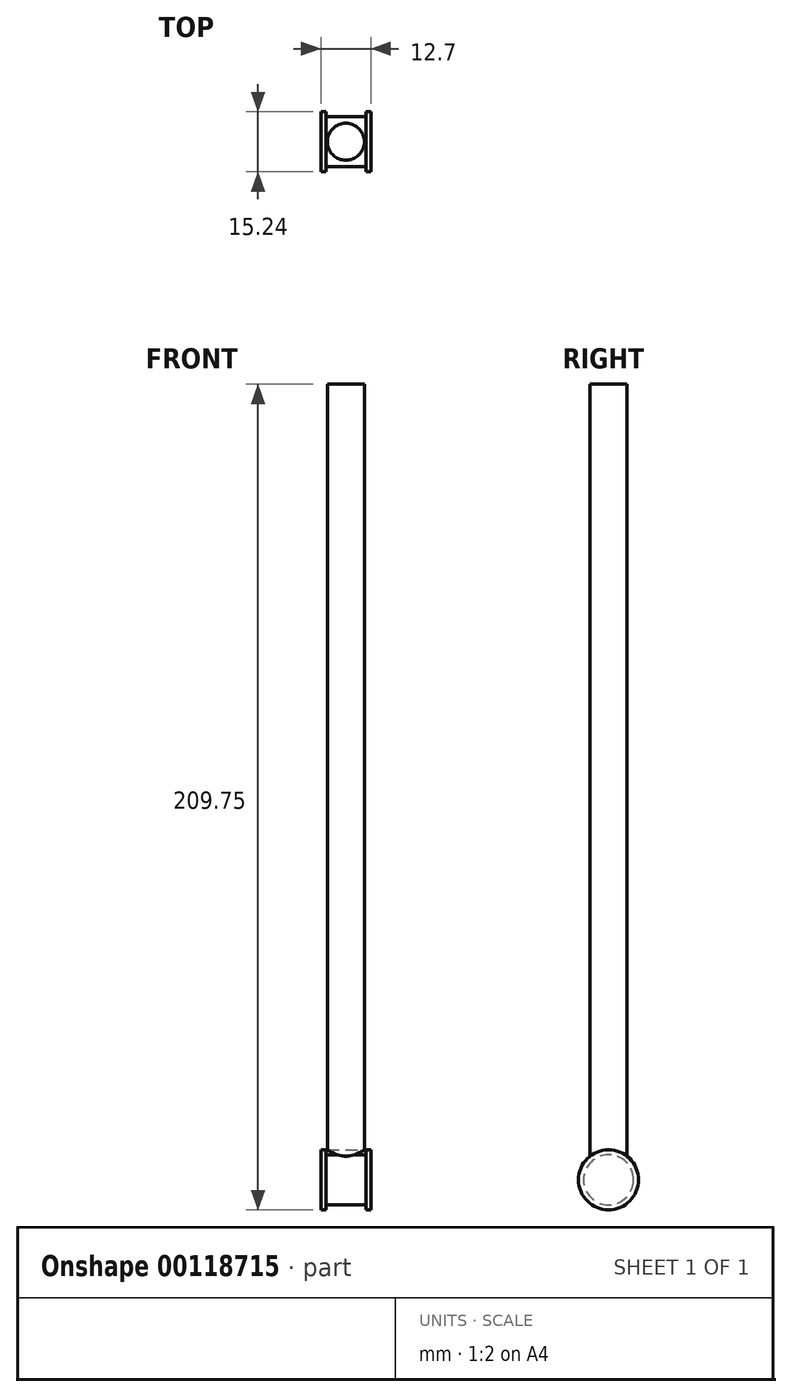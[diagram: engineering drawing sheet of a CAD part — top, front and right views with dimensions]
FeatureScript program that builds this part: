
annotation { "Feature Type Name" : "Feature", "Feature Type Description" : "" }
export const myFeature = defineFeature(function(context is Context, id is Id, definition is map)
    precondition{}
    {
        {
            var Q0;
            Q0=qCreatedBy(makeId("Top.planeOp"),FACE);
            var sketch = newSketch(context, id + "F0", { "sketchPlane" : qUnion([Q0])});
            skCircle(sketch, "E0", {"center": v(0, 0) * mm, "radius": 4.7 * mm});
            skSolve(sketch);
        }
        {
            var Q0;
            Q0 = qSketchRegion(id + "F0", true);
            extrude(context, id + "F1", {"entities" : qUnion([Q0]), "depth" : 196.85 * mm});
        }
        {
            var Q0;
            Q0=qCreatedBy(makeId("Right.planeOp"),FACE);
            var sketch = newSketch(context, id + "F2", { "sketchPlane" : qUnion([Q0])});
            skCircle(sketch, "E1", {"center": v(0, -5.28) * mm, "radius": 7.62 * mm});
            skSolve(sketch);
        }
        {
            var Q0;
            Q0 = qSketchRegion(id + "F2", true);
            extrude(context, id + "F3", {"entities" : qUnion([Q0]), "operationType" : NewBodyOperationType.ADD, "endBound" : BoundingType.SYMMETRIC, "depth" : 12.7 * mm});
        }
        {
            var Q0;
            Q0=qCreatedBy(makeId("Right.planeOp"),FACE);
            var sketch = newSketch(context, id + "F4", { "sketchPlane" : qUnion([Q0])});
            skPoint(sketch, "E2", {"position": v(0, -5.28) * mm});
            skCircle(sketch, "E3", {"center": v(0, -5.28) * mm, "radius": 6.35 * mm});
            skCircle(sketch, "E4.0", {"center": v(0, -5.28) * mm, "radius": 7.62 * mm});
            skSolve(sketch);
        }
        {
            var Q0;
            Q0 = qSketchRegion(id + "F4", true);
            extrude(context, id + "F5", {"entities" : qUnion([Q0]), "operationType" : NewBodyOperationType.REMOVE, "endBound" : BoundingType.SYMMETRIC, "oppositeDirection" : true, "depth" : 10.16 * mm});
        }
    });
